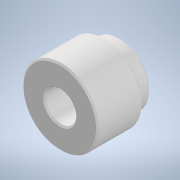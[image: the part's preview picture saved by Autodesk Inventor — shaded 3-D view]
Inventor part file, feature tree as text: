
AUTODESK INVENTOR PART (.ipt)
format: ipt  version: 2021 (Build 250183000, 183)  size: 131,584 bytes
history: native  units: mm
features: other x3, extrude x2, sketch x2, chamfer x1, reference x1
ambient origin geometry x8: Origin, YZ Plane, XZ Plane, XY Plane, X Axis, Y Axis, Z Axis, Center Point
bodies: Body1 (feature_tree)
feature tree (9):
  other  "Bryła1"
  extrude  "Wyciągnięcie proste1"  Depth=20.0mm
  extrude  "Wyciągnięcie proste2"  Depth=10.0mm TaperAngle=0.0deg
  chamfer  "Faza1"  Distance=50.0mm
  sketch  "Szkic1"
  reference  "Odniesienie1"
  sketch  "Szkic2"
  other  "wszystko.iam"
  other  "dekieltop:1"
